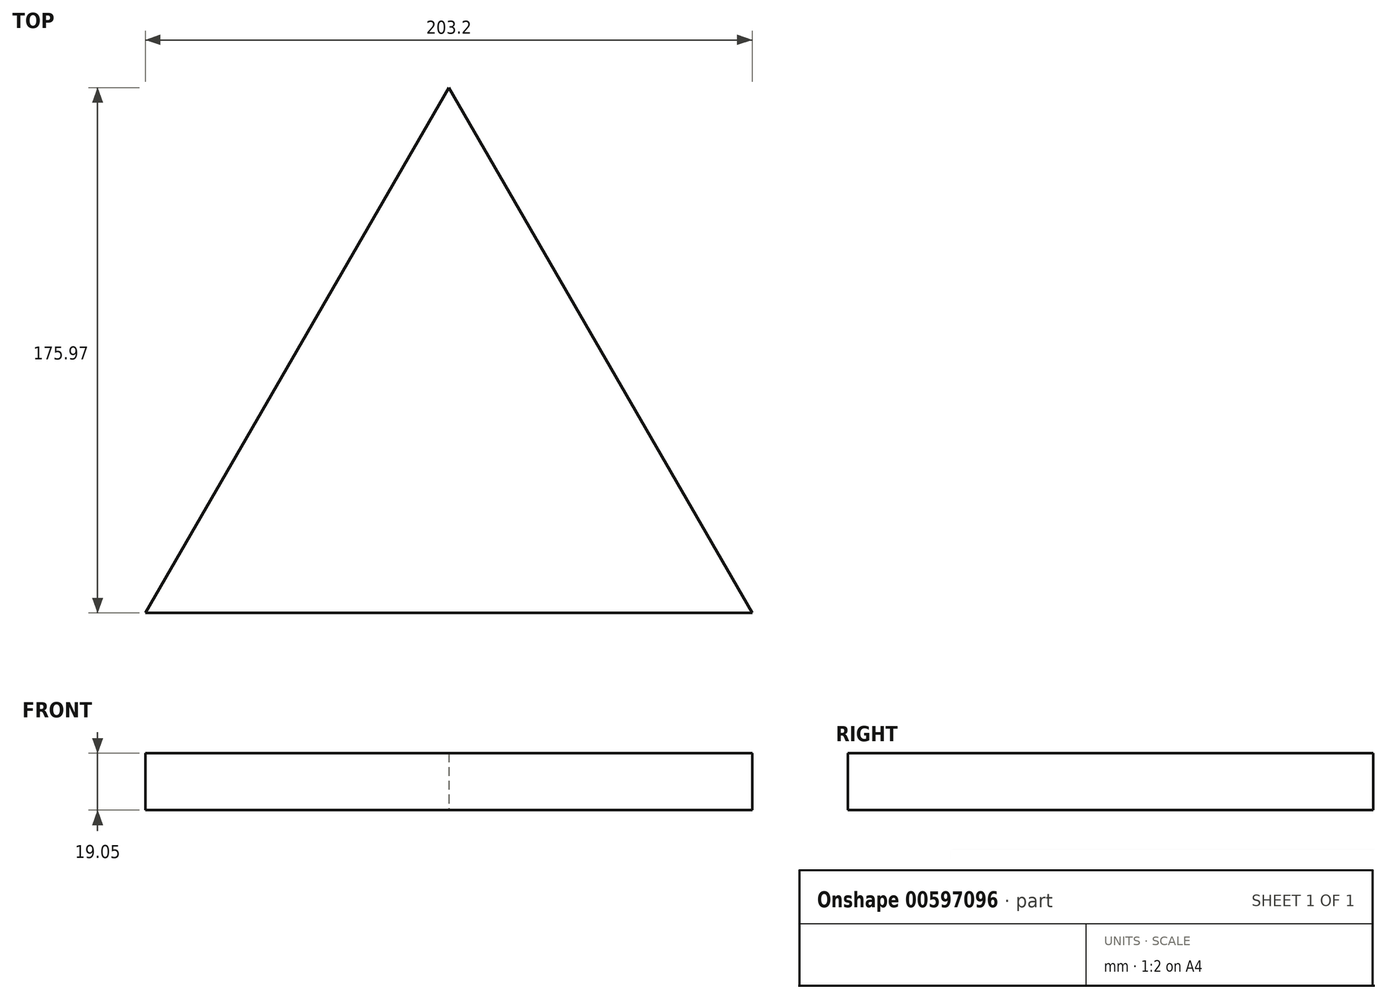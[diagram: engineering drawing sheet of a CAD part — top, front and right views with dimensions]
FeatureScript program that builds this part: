
annotation { "Feature Type Name" : "Feature", "Feature Type Description" : "" }
export const myFeature = defineFeature(function(context is Context, id is Id, definition is map)
    precondition{}
    {
        {
            var Q0;
            Q0=qCreatedBy(makeId("Top.planeOp"),FACE);
            var sketch = newSketch(context, id + "F0", { "sketchPlane" : qUnion([Q0])});
            skLineSegment(sketch, "E0", {"start": v(-43.98, -56.75) * mm, "end": v(159.22, -56.75) * mm});
            skLineSegment(sketch, "E1", {"start": v(-43.98, -56.75) * mm, "end": v(57.62, 119.22) * mm});
            skLineSegment(sketch, "E2", {"start": v(57.62, 119.22) * mm, "end": v(159.22, -56.75) * mm});
            skSolve(sketch);
        }
        {
            var Q0;
            Q0=qCreatedBy(makeId("Top.planeOp"),FACE);
            var sketch = newSketch(context, id + "F1", { "sketchPlane" : qUnion([Q0])});
            skLineSegment(sketch, "E3.0", {"start": v(126.22, -37.7) * mm, "end": v(57.62, 81.12) * mm});
            skLineSegment(sketch, "E3.1", {"start": v(-10.99, -37.7) * mm, "end": v(126.22, -37.7) * mm});
            skLineSegment(sketch, "E3.2", {"start": v(57.62, 81.12) * mm, "end": v(-10.99, -37.7) * mm});
            skSolve(sketch);
        }
        {
            var Q0;
            Q0=makeQuery(id+"F0.imprint","IMPRINT",FACE,{"disambiguationData":[TD([[makeQuery(id+"F0.imprint","IMPRINT",EDGE,{"derivedFrom":sQuery(id+"F0.wireOp",EDGE,"E0")}),1.0]])]});
            extrude(context, id + "F2", {"entities" : qUnion([Q0]), "depth" : 19.05 * mm, "offsetDistance" : 25.4 * mm});
        }
        {
            var Q0;
            Q0=makeQuery(id+"F1.imprint","IMPRINT",FACE,{"disambiguationData":[TD([[makeQuery(id+"F1.imprint","IMPRINT",EDGE,{"derivedFrom":sQuery(id+"F1.wireOp",EDGE,"E3.0")}),1.0]])]});
            var Q1;
            Q1=sQuery(id+"F1.wireOp",EDGE,"E3.0");
            extrude(context, id + "F3", {"entities" : qUnion([Q0]), "operationType" : NewBodyOperationType.REMOVE, "surfaceEntities" : qUnion([Q1]), "oppositeDirection" : true, "depth" : 25.4 * mm, "offsetDistance" : 25.4 * mm});
        }
    });
